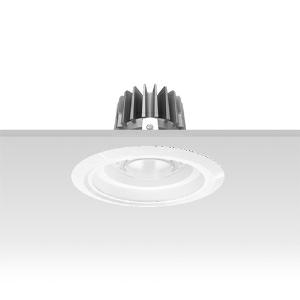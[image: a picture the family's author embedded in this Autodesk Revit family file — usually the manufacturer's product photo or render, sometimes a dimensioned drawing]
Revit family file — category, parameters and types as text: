
# Revit family: 3f_filippi_-_3f_reno_bianco_ampio_3f_filippi_-_30375_a01023_-_3f_reno_150_wh_2000-840_dali_wide___vt_wh_41e3
name_source: partatom
category: Lighting Fixtures
units: mm (PartAtom-declared; Revit-internal decimal feet)

## family parameters
Cut with Voids When Loaded = No
Host = Face
Light Source = No
Part Type = Normal
Room Calculation Point = No
Round Connector Dimension = Use Diameter
Shared = No

## types (1)
- 3F Filippi - 3F Reno Bianco Ampio (1 x LED, 1972 lm, 20 W, 4000 K)
    Apparent Load = 20 VA
    Approval mark = CE
    CIE Flux Codes = 74 93 99 100 100
    Color Rendering = 80
    Color Temperature = 4000 K
    Control Gear = Electronic transformer
    Default Elevation = 1800 mm
    Description = ILLUMINOTECHNICAL
Luminous efficiency 100% (DLOR 100%, ULOR 0%).
Initial luminous flux of the luminaire 1972 lm.
Direct symmetric wide distribution.
Installation Interdistance Transv.D = 1.54 x hu - Long.D = 1.54 x hu.
Tabular UGR (CIE 117 - 4H-8H; S=0.25H; 70/50/20): RUG 23.3 - 23.2.
Beam angle: 74° - 73°.
Luminous efficacy 99 lm/W.
Lifetime (L90/B10): 30000 h. (tq+25°C)
Lifetime (L85/B10): 50000 h. (tq+25°C)
Lifetime (L70/B10): 80000 h. (tq+25°C)
Sudden decreased luminous flux after 50000 hours: 0% (C0).
Photobiological safety in compliance with IEC/TR 62778: RG0 risk exempt, (IEC 62471).
In compliance with IEC/EN 62722-2-1 - IEC/EN 62717 standards.

SOURCE
Compact LED module 2000/840.
Energy efficiency class (UE 2019/2020 - UE 2019/2015): D.
CIE 13.3 Colour rendering index: CRI >80 (R9 <50%).
IES TM-30 Fidelity Index: Rf = 84 Rg = 95.
CCT nominal colour temperature 4000 K.
Colour initial tolerance (MacAdam): SDCM 3.
Zhaga Book 3 compliant.

MECHANICAL
Passive heat dissipator in die-casting aluminium, oversized, for optimum thermal management of the LED module.
Parabolic element with graduated/concentric rings in white polycarbonate.
Transparent external lens with glossy and satin differentiated surfaces, with a cooling and anti-insect system in methacrylate (PMMA).
Fastening spring clips in stainless steel.
Dimensions: diameter 176 mm, height 111 mm. Weight 0.84 kg.
IP44 protection degree for exposed part, IP20 for recessed part.
Mechanical strength to impacts IK06 (1 joule).
Glow-wire test resistance 650°C.

ELECTRICAL
Wiring on a separate unit.
Halogen Free DALI-2 DATI (Parts 251, 252, 253), PUSH-DIM, electronic wiring 230V-50/60Hz, power factor 0.90 at full load, THD <25%, constant output current, SELV, class II, 1 driver, 1 DALI addresse.
Power of the luminaire 20 W.
ENEC - CE.
SAFE FLICKER: PstLM=<1 and SVM=<0.4 (IEC TR 61547-1 and IEC TR 63158), to ensure a more comfortable and safe light.
Luminaire compliant with EN 60598-2-22 for power supply from a centralised emergency system CPSS (Central Power Supply System), not incorporated in the luminaire - high risk areas excluded. The default power and flux are 100% in AC and 100% in DC.
Ambient temperature from 0°C to +25°C.
Temperature class T6 max 85°C.
Relative humidity UR: <85%.

INSTALLATION
Pull-up recessed fitting.
False ceiling carving: 150 mm.
All accessories dedicated to this product are available on the Catalog and on our website www.3F-Filippi.com.

ACCESSORIES
A01023 - VT transparent glass, tempered, not flammable, locked and in line with the trim, in white polycarbonate.

APPLICATIONS
Environments: architectural, commercial, exhibition areas, transit areas, corridors, shops, display windows, service areas.
In false ceilings with narrow voids.

LIGHT MANAGEMENT
Recommended minimum setting: 10%.
The luminaire, equipped with (DALI-2 DATI) driver, can be controlled manually with 3F Easy Dim technology or automatically/manually with wired or wireless DALI/D2D control systems.
The D2D driver guarantees interoperability with other devices with the same certification by making the following information available:
Device Data (Part 251), Energy Report (Part 252), Diagnosis & Maintenance (Part 253).
In electrical systems without a regulation system (manual or automatic) and DALI bus, a suitable jumper must be made on the DA-DA terminals of the appliance.

WARNING
Luminaire designed for disposal/recycling at end-of-life.
Replaceable (LED only) light source by a professional. Replaceable control gear by a professional.
    Height = 0 mm  [stored 0 ft]
    Lamp = 1 x LED
    Lamp Light Flux = 1972 lm
    Lamp Power = 20 W
    Lamp count = 1
    Length = 176 mm
    Lifetime = 50000 h
    Luminous efficacy = 99 lm/W
    Manufacturer = 3F Filippi
    ModVariant = No
    Model = 3F Filippi - 30375+A01023 - 3F Reno 150 WH 2000-840 DALI WIDE + VT WH
    Mounting Place = Ceiling
    Mounting Type = Recessed
    Number of Poles = 1
    OnlyDefault = Yes
    Power Factor = 1
    Product Name = 3F Filippi - 3F Reno Bianco Ampio
    Product group = recessed luminaire
    ProductGroupID = 4
    Protection Class = Protection class II
    Protection Degree = IP 20
    RLX_Detail_Level = 1
    RLX_Emergency_Light_Flux = 0 lm
    RLX_Emergency_Type = 0
    RLX_Emergency_Type_DB = No
    RlxData = <blob elided: 84001 chars, md5=3038fc3d>
    Socket = socket
    Standby Power = 0 W
    System Light Flux = 1972 lm
    System Power = 20 W
    Type Comments = Product without accessories
    Type Image = 3ffilippi_3f_reno_150_wh_d100__a01023.jpg
    URL = http://relux.com
    VarID = ---
    Voltage = 0 V
    Weight = 0.00 kg
    Width = 0 mm  [stored 0 ft]

note: [stored X ft] marks values corroborated as IEEE doubles in the binary element streams (Revit-internal decimal feet)

## geometry (parser evidence)
native form markers: Blend x4, Sweep x10
no freeform markers — native parametric forms only
